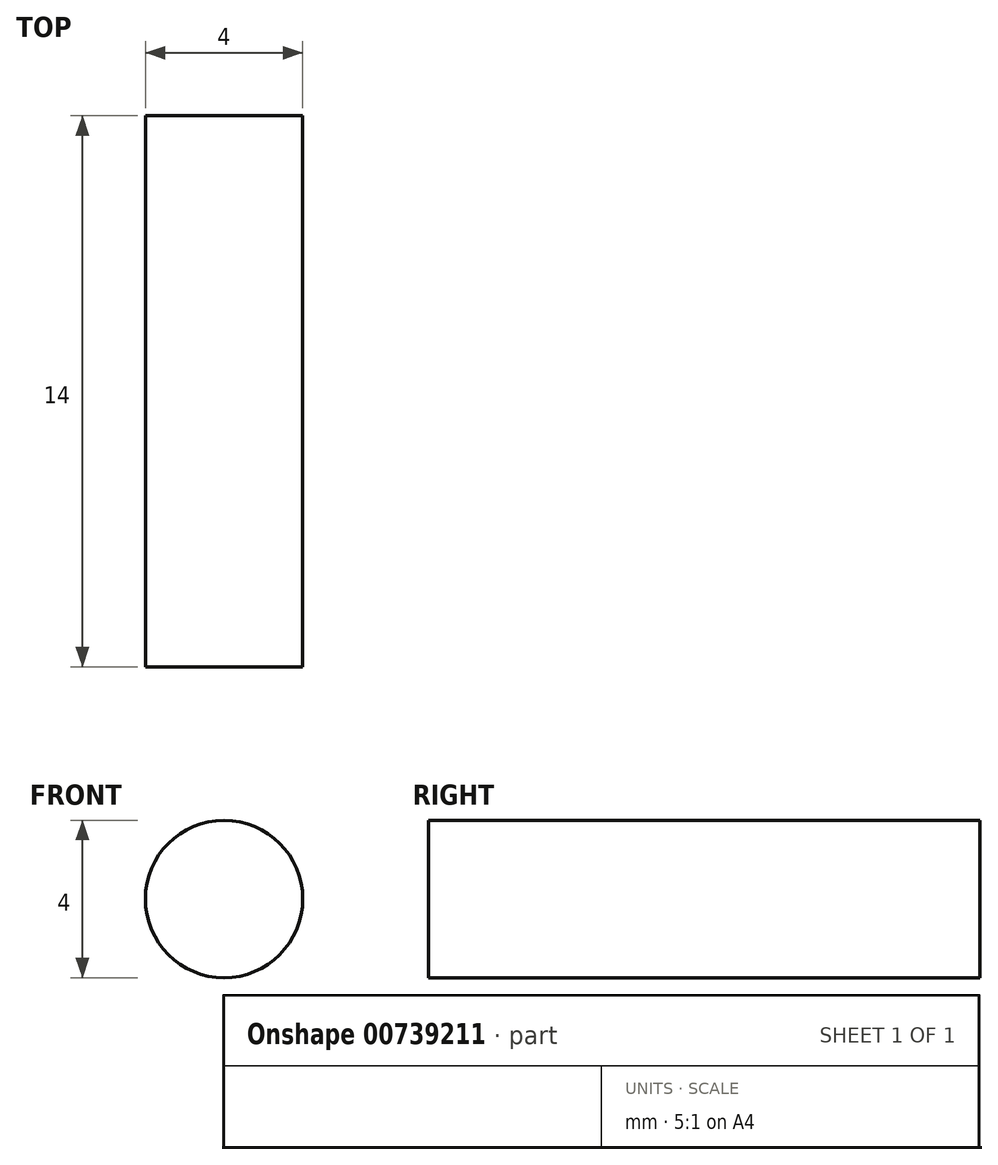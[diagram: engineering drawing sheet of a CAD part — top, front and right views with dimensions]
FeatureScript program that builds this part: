
annotation { "Feature Type Name" : "Feature", "Feature Type Description" : "" }
export const myFeature = defineFeature(function(context is Context, id is Id, definition is map)
    precondition{}
    {
        {
            var Q0;
            Q0=qCreatedBy(makeId("Front.planeOp"),FACE);
            var sketch = newSketch(context, id + "F0", { "sketchPlane" : qUnion([Q0])});
            skCircle(sketch, "E0", {"center": v(0, 0) * mm, "radius": 2 * mm});
            skSolve(sketch);
        }
        {
            var Q0;
            Q0 = qSketchRegion(id + "F0", true);
            extrude(context, id + "F1", {"entities" : qUnion([Q0]), "depth" : 14 * mm, "offsetDistance" : 25.4 * mm});
        }
    });
